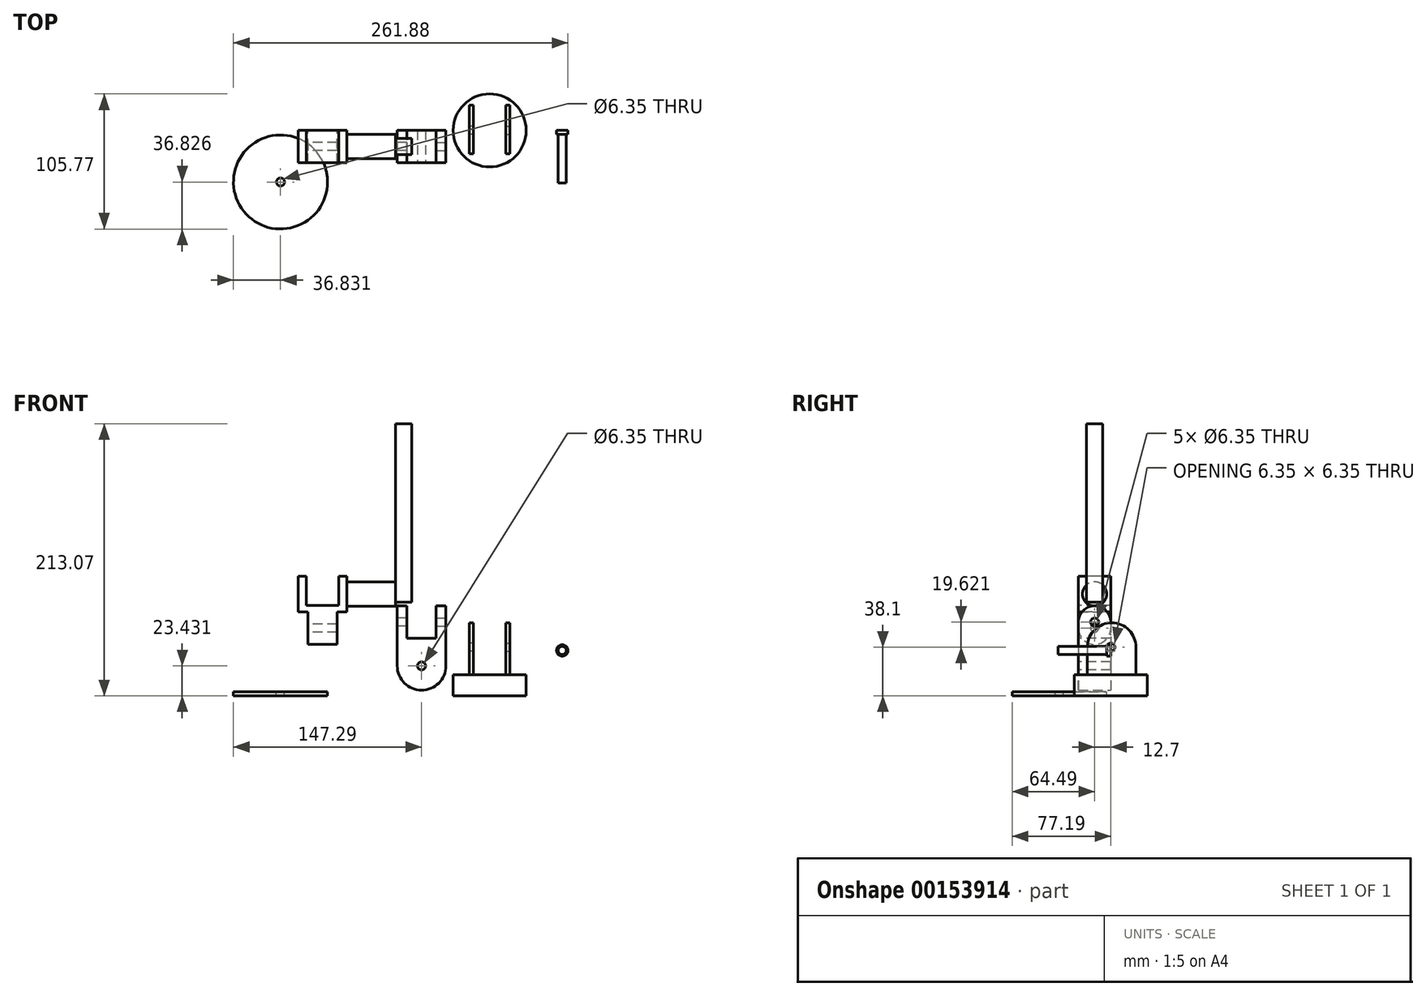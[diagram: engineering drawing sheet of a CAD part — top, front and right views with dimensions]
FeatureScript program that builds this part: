
annotation { "Feature Type Name" : "Feature", "Feature Type Description" : "" }
export const myFeature = defineFeature(function(context is Context, id is Id, definition is map)
    precondition{}
    {
        {
            var Q0;
            Q0=qCreatedBy(makeId("Top.planeOp"),FACE);
            var sketch = newSketch(context, id + "F0", { "sketchPlane" : qUnion([Q0])});
            skCircle(sketch, "E0", {"center": v(0, 0) * mm, "radius": 28.58 * mm});
            skSolve(sketch);
        }
        {
            var Q0;
            Q0 = qSketchRegion(id + "F0", true);
            extrude(context, id + "F1", {"entities" : qUnion([Q0]), "depth" : 16.5 * mm});
        }
        {
            var Q0;
            Q0=makeQuery(id+"F1.opExtrude","CAP_FACE",FACE,{"disambiguationData":[OSD([sQuery(id+"F0.wireOp",EDGE,"E0")])],"isStart":false});
            var sketch = newSketch(context, id + "F2", { "sketchPlane" : qUnion([Q0])});
            skLineSegment(sketch, "E1", {"start": v(-12.7, 19.69) * mm, "end": v(-12.7, -18.42) * mm});
            skLineSegment(sketch, "E2", {"start": v(-12.7, 19.69) * mm, "end": v(-15.88, 19.69) * mm});
            skLineSegment(sketch, "E3", {"start": v(-15.88, 19.69) * mm, "end": v(-15.88, -18.41) * mm});
            skLineSegment(sketch, "E4", {"start": v(-15.88, -18.42) * mm, "end": v(-12.7, -18.42) * mm});
            skLineSegment(sketch, "E5", {"start": v(12.7, -18.41) * mm, "end": v(12.7, 19.69) * mm});
            skLineSegment(sketch, "E6", {"start": v(12.7, 19.69) * mm, "end": v(15.88, 19.69) * mm});
            skLineSegment(sketch, "E7", {"start": v(15.88, 19.69) * mm, "end": v(15.88, -18.41) * mm});
            skLineSegment(sketch, "E8", {"start": v(15.88, -18.41) * mm, "end": v(12.7, -18.41) * mm});
            skSolve(sketch);
        }
        {
            var Q0;
            Q0 = qSketchRegion(id + "F2", true);
            extrude(context, id + "F3", {"entities" : qUnion([Q0]), "operationType" : NewBodyOperationType.ADD, "depth" : 21.59 * mm});
        }
        {
            var Q0;
            Q0=makeQuery(id+"F3.opExtrude","SWEPT_FACE",FACE,{"disambiguationData":[OSD([sQuery(id+"F2.wireOp",EDGE,"E3")])]});
            var sketch = newSketch(context, id + "F4", { "sketchPlane" : qUnion([Q0])});
            skArc(sketch, "E9", {"start": v(18.42, 38.1) * mm, "mid": v(-0.63, 57.15) * mm, "end": v(-19.69, 38.1) * mm});
            skSolve(sketch);
        }
        {
            var Q0;
            Q0=makeQuery(id+"F4.imprint","IMPRINT",FACE,{"disambiguationData":[TD([[makeQuery(id+"F4.imprint","IMPRINT",EDGE,{"derivedFrom":sQuery(id+"F4.wireOp",EDGE,"E9")}),1.0]])]});
            extrude(context, id + "F5", {"entities" : qUnion([Q0]), "operationType" : NewBodyOperationType.ADD, "oppositeDirection" : true, "depth" : 3.17 * mm});
        }
        {
            var Q0;
            Q0=makeQuery(id+"F3.opExtrude","SWEPT_FACE",FACE,{"disambiguationData":[OSD([sQuery(id+"F2.wireOp",EDGE,"E7")])]});
            var sketch = newSketch(context, id + "F6", { "sketchPlane" : qUnion([Q0])});
            skArc(sketch, "E10", {"start": v(19.68, 38.1) * mm, "mid": v(0.63, 57.15) * mm, "end": v(-18.42, 38.1) * mm});
            skSolve(sketch);
        }
        {
            var Q0;
            Q0=makeQuery(id+"F6.imprint","IMPRINT",FACE,{"disambiguationData":[TD([[makeQuery(id+"F6.imprint","IMPRINT",EDGE,{"derivedFrom":sQuery(id+"F6.wireOp",EDGE,"E10")}),1.0]])]});
            extrude(context, id + "F7", {"entities" : qUnion([Q0]), "operationType" : NewBodyOperationType.ADD, "oppositeDirection" : true, "depth" : 3.17 * mm});
        }
        {
            var Q0;
            {var subQ0=sQuery(id+"F2.wireOp",EDGE,"E7");Q0=makeQuery(id+"F7.boolean.opBoolean","MERGE",FACE,{"derivedFrom":[makeQuery(id+"F3.opExtrude","SWEPT_FACE",FACE,{"disambiguationData":[OSD([subQ0])]}),makeQuery(id+"F7.opExtrude","CAP_FACE",FACE,{"disambiguationData":[OSD([subQ0,sQuery(id+"F6.wireOp",EDGE,"E10")])],"isStart":true})]});}
            var sketch = newSketch(context, id + "F8", { "sketchPlane" : qUnion([Q0])});
            skCircle(sketch, "E11", {"center": v(0, 38.1) * mm, "radius": 3.18 * mm});
            skSolve(sketch);
        }
        {
            var Q0;
            Q0 = qSketchRegion(id + "F8", true);
            extrude(context, id + "F9", {"entities" : qUnion([Q0]), "operationType" : NewBodyOperationType.REMOVE, "oppositeDirection" : true, "depth" : 25.4 * mm});
        }
        {
            var Q0;
            {var subQ0=sQuery(id+"F2.wireOp",EDGE,"E3");Q0=makeQuery(id+"F5.boolean.opBoolean","MERGE",FACE,{"derivedFrom":[makeQuery(id+"F3.opExtrude","SWEPT_FACE",FACE,{"disambiguationData":[OSD([subQ0])]}),makeQuery(id+"F5.opExtrude","CAP_FACE",FACE,{"disambiguationData":[OSD([subQ0,sQuery(id+"F4.wireOp",EDGE,"E9")])],"isStart":true})]});}
            var sketch = newSketch(context, id + "F10", { "sketchPlane" : qUnion([Q0])});
            skCircle(sketch, "E12", {"center": v(0, 38.1) * mm, "radius": 3.18 * mm});
            skSolve(sketch);
        }
        {
            var Q0;
            Q0 = qSketchRegion(id + "F10", true);
            extrude(context, id + "F11", {"entities" : qUnion([Q0]), "operationType" : NewBodyOperationType.REMOVE, "oppositeDirection" : true, "depth" : 25.4 * mm});
        }
        {
            var Q0;
            Q0=qCreatedBy(makeId("Front.planeOp"),FACE);
            var sketch = newSketch(context, id + "F12", { "sketchPlane" : qUnion([Q0])});
            skLineSegment(sketch, "E13.bottom", {"start": v(-72.39, 57.72) * mm, "end": v(-34.29, 57.72) * mm});
            skLineSegment(sketch, "E13.top", {"start": v(-72.39, 23.43) * mm, "end": v(-34.29, 23.43) * mm});
            skLineSegment(sketch, "E13.left", {"start": v(-72.39, 57.72) * mm, "end": v(-72.39, 23.43) * mm});
            skLineSegment(sketch, "E13.right", {"start": v(-34.29, 57.72) * mm, "end": v(-34.29, 23.43) * mm});
            skArc(sketch, "E14", {"start": v(-72.39, 23.43) * mm, "mid": v(-53.34, 4.38) * mm, "end": v(-34.29, 23.43) * mm});
            skSolve(sketch);
        }
        {
            var Q0;
            Q0 = qSketchRegion(id + "F12", true);
            extrude(context, id + "F13", {"entities" : qUnion([Q0]), "depth" : 25.4 * mm});
        }
        {
            var Q0;
            Q0=makeQuery(id+"F13.opExtrude","CAP_FACE",FACE,{"disambiguationData":[OSD([sQuery(id+"F12.wireOp",EDGE,"E13.bottom"),sQuery(id+"F12.wireOp",EDGE,"E13.left"),sQuery(id+"F12.wireOp",EDGE,"E13.right"),sQuery(id+"F12.wireOp",EDGE,"E14")])],"isStart":false});
            var sketch = newSketch(context, id + "F14", { "sketchPlane" : qUnion([Q0])});
            skCircle(sketch, "E15", {"center": v(-53.34, 23.43) * mm, "radius": 3.18 * mm});
            skSolve(sketch);
        }
        {
            var Q0;
            Q0 = qSketchRegion(id + "F14", true);
            extrude(context, id + "F15", {"entities" : qUnion([Q0]), "operationType" : NewBodyOperationType.REMOVE, "oppositeDirection" : true, "depth" : 25.4 * mm});
        }
        {
            var Q0;
            Q0=makeQuery(id+"F13.opExtrude","CAP_FACE",FACE,{"disambiguationData":[OSD([sQuery(id+"F12.wireOp",EDGE,"E13.bottom"),sQuery(id+"F12.wireOp",EDGE,"E13.left"),sQuery(id+"F12.wireOp",EDGE,"E13.right"),sQuery(id+"F12.wireOp",EDGE,"E14")])],"isStart":false});
            var sketch = newSketch(context, id + "F16", { "sketchPlane" : qUnion([Q0])});
            skLineSegment(sketch, "E16.bottom", {"start": v(-64.77, 57.72) * mm, "end": v(-41.9, 57.72) * mm});
            skLineSegment(sketch, "E16.top", {"start": v(-64.77, 45.02) * mm, "end": v(-41.9, 45.02) * mm});
            skLineSegment(sketch, "E16.left", {"start": v(-64.77, 57.72) * mm, "end": v(-64.77, 45.02) * mm});
            skLineSegment(sketch, "E16.right", {"start": v(-41.9, 57.72) * mm, "end": v(-41.9, 45.02) * mm});
            skSolve(sketch);
        }
        {
            var Q0;
            Q0 = qSketchRegion(id + "F16", true);
            extrude(context, id + "F17", {"entities" : qUnion([Q0]), "operationType" : NewBodyOperationType.REMOVE, "oppositeDirection" : true, "depth" : 25.4 * mm});
        }
        {
            var Q0;
            Q0=makeQuery(id+"F13.opExtrude","SWEPT_FACE",FACE,{"disambiguationData":[OSD([sQuery(id+"F12.wireOp",EDGE,"E13.left")])]});
            var sketch = newSketch(context, id + "F18", { "sketchPlane" : qUnion([Q0])});
            skArc(sketch, "E17", {"start": v(25.4, 57.72) * mm, "mid": v(12.7, 70.42) * mm, "end": v(0, 57.72) * mm});
            skSolve(sketch);
        }
        {
            var Q0;
            Q0=makeQuery(id+"F18.imprint","IMPRINT",FACE,{"disambiguationData":[TD([[makeQuery(id+"F18.imprint","IMPRINT",EDGE,{"derivedFrom":sQuery(id+"F18.wireOp",EDGE,"E17")}),1.0]])]});
            extrude(context, id + "F19", {"entities" : qUnion([Q0]), "operationType" : NewBodyOperationType.ADD, "oppositeDirection" : true, "depth" : 7.62 * mm});
        }
        {
            var Q0;
            Q0=makeQuery(id+"F13.opExtrude","SWEPT_FACE",FACE,{"disambiguationData":[OSD([sQuery(id+"F12.wireOp",EDGE,"E13.right")])]});
            var sketch = newSketch(context, id + "F20", { "sketchPlane" : qUnion([Q0])});
            skArc(sketch, "E18", {"start": v(0, 57.72) * mm, "mid": v(-12.7, 70.42) * mm, "end": v(-25.4, 57.72) * mm});
            skSolve(sketch);
        }
        {
            var Q0;
            Q0=makeQuery(id+"F20.imprint","IMPRINT",FACE,{"disambiguationData":[TD([[makeQuery(id+"F20.imprint","IMPRINT",EDGE,{"derivedFrom":sQuery(id+"F20.wireOp",EDGE,"E18")}),1.0]])]});
            extrude(context, id + "F21", {"entities" : qUnion([Q0]), "operationType" : NewBodyOperationType.ADD, "oppositeDirection" : true, "depth" : 7.62 * mm});
        }
        {
            var Q0;
            {var subQ0=sQuery(id+"F12.wireOp",EDGE,"E13.left");Q0=makeQuery(id+"F19.boolean.opBoolean","MERGE",FACE,{"derivedFrom":[makeQuery(id+"F13.opExtrude","SWEPT_FACE",FACE,{"disambiguationData":[OSD([subQ0])]}),makeQuery(id+"F19.opExtrude","CAP_FACE",FACE,{"disambiguationData":[OSD([sQuery(id+"F12.wireOp",EDGE,"E13.bottom"),subQ0,sQuery(id+"F18.wireOp",EDGE,"E17")])],"isStart":true})]});}
            var sketch = newSketch(context, id + "F22", { "sketchPlane" : qUnion([Q0])});
            skCircle(sketch, "E19", {"center": v(12.7, 57.72) * mm, "radius": 3.18 * mm});
            skSolve(sketch);
        }
        {
            var Q0;
            Q0 = qSketchRegion(id + "F22", true);
            extrude(context, id + "F23", {"entities" : qUnion([Q0]), "operationType" : NewBodyOperationType.REMOVE, "oppositeDirection" : true, "depth" : 12.7 * mm});
        }
        {
            var Q0;
            {var subQ0=sQuery(id+"F12.wireOp",EDGE,"E13.right");Q0=makeQuery(id+"F21.boolean.opBoolean","MERGE",FACE,{"derivedFrom":[makeQuery(id+"F13.opExtrude","SWEPT_FACE",FACE,{"disambiguationData":[OSD([subQ0])]}),makeQuery(id+"F21.opExtrude","CAP_FACE",FACE,{"disambiguationData":[OSD([sQuery(id+"F12.wireOp",EDGE,"E13.bottom"),subQ0,sQuery(id+"F20.wireOp",EDGE,"E18")])],"isStart":true})]});}
            var sketch = newSketch(context, id + "F24", { "sketchPlane" : qUnion([Q0])});
            skCircle(sketch, "E20", {"center": v(-12.7, 57.72) * mm, "radius": 3.18 * mm});
            skSolve(sketch);
        }
        {
            var Q0;
            Q0 = qSketchRegion(id + "F24", true);
            extrude(context, id + "F25", {"entities" : qUnion([Q0]), "operationType" : NewBodyOperationType.REMOVE, "oppositeDirection" : true, "depth" : 25.4 * mm});
        }
        {
            var Q0;
            Q0=qCreatedBy(makeId("Front.planeOp"),FACE);
            var sketch = newSketch(context, id + "F26", { "sketchPlane" : qUnion([Q0])});
            skLineSegment(sketch, "E21.bottom", {"start": v(-142.33, 65.75) * mm, "end": v(-119.47, 65.75) * mm});
            skLineSegment(sketch, "E21.top", {"start": v(-142.33, 53.05) * mm, "end": v(-119.47, 53.05) * mm});
            skLineSegment(sketch, "E21.left", {"start": v(-142.33, 65.75) * mm, "end": v(-142.33, 53.05) * mm});
            skLineSegment(sketch, "E21.right", {"start": v(-119.47, 65.75) * mm, "end": v(-119.47, 53.05) * mm});
            skSolve(sketch);
        }
        {
            var Q0;
            Q0 = qSketchRegion(id + "F26", true);
            extrude(context, id + "F27", {"entities" : qUnion([Q0]), "depth" : 25.4 * mm});
        }
        {
            var Q0;
            Q0=makeQuery(id+"F27.opExtrude","SWEPT_FACE",FACE,{"disambiguationData":[OSD([sQuery(id+"F26.wireOp",EDGE,"E21.right")])]});
            var sketch = newSketch(context, id + "F28", { "sketchPlane" : qUnion([Q0])});
            skArc(sketch, "E22", {"start": v(-25.4, 53.05) * mm, "mid": v(-12.7, 40.35) * mm, "end": v(0, 53.05) * mm});
            skSolve(sketch);
        }
        {
            var Q0;
            Q0=makeQuery(id+"F28.imprint","IMPRINT",FACE,{"disambiguationData":[TD([[makeQuery(id+"F28.imprint","IMPRINT",EDGE,{"derivedFrom":sQuery(id+"F28.wireOp",EDGE,"E22")}),1.0]])]});
            extrude(context, id + "F29", {"entities" : qUnion([Q0]), "operationType" : NewBodyOperationType.ADD, "oppositeDirection" : true, "depth" : 22.86 * mm});
        }
        {
            var Q0;
            Q0=makeQuery(id+"F29.boolean.opBoolean","MERGE",FACE,{"derivedFrom":[makeQuery(id+"F27.opExtrude","SWEPT_FACE",FACE,{"disambiguationData":[OSD([sQuery(id+"F26.wireOp",EDGE,"E21.left")])]}),makeQuery(id+"F29.opExtrude","CAP_FACE",FACE,{"disambiguationData":[OSD([sQuery(id+"F26.wireOp",EDGE,"E21.top"),sQuery(id+"F26.wireOp",EDGE,"E21.right"),sQuery(id+"F28.wireOp",EDGE,"E22")])],"isStart":false})]});
            var sketch = newSketch(context, id + "F30", { "sketchPlane" : qUnion([Q0])});
            skCircle(sketch, "E23", {"center": v(12.7, 53.05) * mm, "radius": 3.18 * mm});
            skSolve(sketch);
        }
        {
            var Q0;
            Q0 = qSketchRegion(id + "F30", true);
            extrude(context, id + "F31", {"entities" : qUnion([Q0]), "operationType" : NewBodyOperationType.REMOVE, "oppositeDirection" : true, "depth" : 25.4 * mm});
        }
        {
            var Q0;
            Q0=makeQuery(id+"F27.opExtrude","CAP_FACE",FACE,{"disambiguationData":[OSD([sQuery(id+"F26.wireOp",EDGE,"E21.bottom"),sQuery(id+"F26.wireOp",EDGE,"E21.top"),sQuery(id+"F26.wireOp",EDGE,"E21.left"),sQuery(id+"F26.wireOp",EDGE,"E21.right")])],"isStart":false});
            var sketch = newSketch(context, id + "F32", { "sketchPlane" : qUnion([Q0])});
            skLineSegment(sketch, "E24.bottom", {"start": v(-149.95, 65.75) * mm, "end": v(-111.85, 65.75) * mm});
            skLineSegment(sketch, "E24.top", {"start": v(-149.95, 70.83) * mm, "end": v(-111.85, 70.83) * mm});
            skLineSegment(sketch, "E24.left", {"start": v(-149.95, 65.75) * mm, "end": v(-149.95, 70.83) * mm});
            skLineSegment(sketch, "E24.right", {"start": v(-111.85, 65.75) * mm, "end": v(-111.85, 70.83) * mm});
            skSolve(sketch);
        }
        {
            var Q0;
            Q0 = qSketchRegion(id + "F32", true);
            extrude(context, id + "F33", {"entities" : qUnion([Q0]), "operationType" : NewBodyOperationType.ADD, "oppositeDirection" : true, "depth" : 25.4 * mm});
        }
        {
            var Q0;
            Q0=makeQuery(id+"F33.opExtrude","SWEPT_FACE",FACE,{"disambiguationData":[OSD([sQuery(id+"F32.wireOp",EDGE,"E24.top")])]});
            var sketch = newSketch(context, id + "F34", { "sketchPlane" : qUnion([Q0])});
            skLineSegment(sketch, "E25.bottom", {"start": v(-149.95, 0) * mm, "end": v(-143.6, 0) * mm});
            skLineSegment(sketch, "E25.top", {"start": v(-149.95, -25.4) * mm, "end": v(-143.6, -25.4) * mm});
            skLineSegment(sketch, "E25.left", {"start": v(-149.95, 0) * mm, "end": v(-149.95, -25.4) * mm});
            skLineSegment(sketch, "E25.right", {"start": v(-143.6, 0) * mm, "end": v(-143.6, -25.4) * mm});
            skSolve(sketch);
        }
        {
            var Q0;
            Q0 = qSketchRegion(id + "F34", true);
            extrude(context, id + "F35", {"entities" : qUnion([Q0]), "operationType" : NewBodyOperationType.ADD, "depth" : 22.86 * mm});
        }
        {
            var Q0;
            Q0=makeQuery(id+"F33.opExtrude","SWEPT_FACE",FACE,{"disambiguationData":[OSD([sQuery(id+"F32.wireOp",EDGE,"E24.top")])]});
            var sketch = newSketch(context, id + "F36", { "sketchPlane" : qUnion([Q0])});
            skLineSegment(sketch, "E26.bottom", {"start": v(-111.85, 0) * mm, "end": v(-118.2, 0) * mm});
            skLineSegment(sketch, "E26.top", {"start": v(-111.85, -25.4) * mm, "end": v(-118.2, -25.4) * mm});
            skLineSegment(sketch, "E26.left", {"start": v(-111.85, 0) * mm, "end": v(-111.85, -25.4) * mm});
            skLineSegment(sketch, "E26.right", {"start": v(-118.2, 0) * mm, "end": v(-118.2, -25.4) * mm});
            skSolve(sketch);
        }
        {
            var Q0;
            Q0 = qSketchRegion(id + "F36", true);
            extrude(context, id + "F37", {"entities" : qUnion([Q0]), "operationType" : NewBodyOperationType.ADD, "depth" : 22.86 * mm});
        }
        {
            var Q0;
            Q0=qCreatedBy(makeId("Top.planeOp"),FACE);
            var sketch = newSketch(context, id + "F38", { "sketchPlane" : qUnion([Q0])});
            skCircle(sketch, "E27", {"center": v(-163.8, -40.36) * mm, "radius": 36.83 * mm});
            skSolve(sketch);
        }
        {
            var Q0;
            Q0 = qSketchRegion(id + "F38", true);
            extrude(context, id + "F39", {"entities" : qUnion([Q0]), "depth" : 3.3 * mm});
        }
        {
            var Q0;
            Q0=makeQuery(id+"F39.opExtrude","CAP_FACE",FACE,{"disambiguationData":[OSD([sQuery(id+"F38.wireOp",EDGE,"E27")])],"isStart":false});
            var sketch = newSketch(context, id + "F40", { "sketchPlane" : qUnion([Q0])});
            skCircle(sketch, "E28", {"center": v(-163.8, -40.36) * mm, "radius": 3.18 * mm});
            skSolve(sketch);
        }
        {
            var Q0;
            Q0 = qSketchRegion(id + "F40", true);
            extrude(context, id + "F41", {"entities" : qUnion([Q0]), "operationType" : NewBodyOperationType.REMOVE, "oppositeDirection" : true, "depth" : 25.4 * mm});
        }
        {
            var Q0;
            Q0=qCreatedBy(makeId("Front.planeOp"),FACE);
            var sketch = newSketch(context, id + "F42", { "sketchPlane" : qUnion([Q0])});
            skCircle(sketch, "E29", {"center": v(56.8, 35.48) * mm, "radius": 4.45 * mm});
            skSolve(sketch);
        }
        {
            var Q0;
            Q0 = qSketchRegion(id + "F42", true);
            extrude(context, id + "F43", {"entities" : qUnion([Q0]), "depth" : 3.17 * mm});
        }
        {
            var Q0;
            Q0=makeQuery(id+"F43.opExtrude","CAP_FACE",FACE,{"disambiguationData":[OSD([sQuery(id+"F42.wireOp",EDGE,"E29")])],"isStart":false});
            var sketch = newSketch(context, id + "F44", { "sketchPlane" : qUnion([Q0])});
            skCircle(sketch, "E30", {"center": v(56.8, 35.48) * mm, "radius": 3.18 * mm});
            skSolve(sketch);
        }
        {
            var Q0;
            Q0 = qSketchRegion(id + "F44", true);
            extrude(context, id + "F45", {"entities" : qUnion([Q0]), "operationType" : NewBodyOperationType.ADD, "depth" : 38.1 * mm});
        }
        {
            var Q0;
            Q0=makeQuery(id+"F37.boolean.opBoolean","MERGE",FACE,{"derivedFrom":[makeQuery(id+"F33.opExtrude","SWEPT_FACE",FACE,{"disambiguationData":[OSD([sQuery(id+"F32.wireOp",EDGE,"E24.right")])]}),makeQuery(id+"F37.opExtrude","SWEPT_FACE",FACE,{"disambiguationData":[OSD([sQuery(id+"F36.wireOp",EDGE,"E26.left")])]})]});
            var sketch = newSketch(context, id + "F46", { "sketchPlane" : qUnion([Q0])});
            skCircle(sketch, "E31", {"center": v(-12.7, 79.72) * mm, "radius": 9.53 * mm});
            skPoint(sketch, "E31.centerSnap0", {"position": v(-12.7, 93.69) * mm});
            skPoint(sketch, "E31.centerSnap1", {"position": v(-25.4, 79.72) * mm});
            skSolve(sketch);
        }
        {
            var Q0;
            Q0 = qSketchRegion(id + "F46", true);
            extrude(context, id + "F47", {"entities" : qUnion([Q0]), "depth" : 38.1 * mm});
        }
        {
            var Q0;
            Q0=makeQuery(id+"F47.opExtrude","CAP_FACE",FACE,{"disambiguationData":[OSD([sQuery(id+"F46.wireOp",EDGE,"E31")])],"isStart":false});
            var sketch = newSketch(context, id + "F48", { "sketchPlane" : qUnion([Q0])});
            skLineSegment(sketch, "E32.bottom", {"start": v(-6.35, 86.07) * mm, "end": v(-19.05, 86.07) * mm});
            skLineSegment(sketch, "E32.top", {"start": v(-6.35, 73.37) * mm, "end": v(-19.05, 73.37) * mm});
            skLineSegment(sketch, "E32.left", {"start": v(-6.35, 86.07) * mm, "end": v(-6.35, 73.37) * mm});
            skLineSegment(sketch, "E32.right", {"start": v(-19.05, 86.07) * mm, "end": v(-19.05, 73.37) * mm});
            skPoint(sketch, "E32.middle", {"position": v(-12.7, 79.72) * mm});
            skSolve(sketch);
        }
        {
            var Q0;
            Q0 = qSketchRegion(id + "F48", true);
            extrude(context, id + "F49", {"entities" : qUnion([Q0]), "operationType" : NewBodyOperationType.ADD, "depth" : 12.7 * mm});
        }
        {
            var Q0;
            Q0=makeQuery(id+"F49.opExtrude","SWEPT_FACE",FACE,{"disambiguationData":[OSD([sQuery(id+"F48.wireOp",EDGE,"E32.bottom")])]});
            var sketch = newSketch(context, id + "F50", { "sketchPlane" : qUnion([Q0])});
            skCircle(sketch, "E33", {"center": v(-67.4, -12.7) * mm, "radius": 6.35 * mm});
            skPoint(sketch, "E33.centerSnap0", {"position": v(-61.05, -12.7) * mm});
            skPoint(sketch, "E33.centerSnap1", {"position": v(-67.4, -19.05) * mm});
            skSolve(sketch);
        }
        {
            var Q0;
            {var subQ0=sQuery(id+"F50.wireOp",EDGE,"E33");var subQ1=sQuery(id+"F48.wireOp",EDGE,"E32.bottom");var subQ3=makeQuery(id+"F50.imprint","INTERSECT",VERTEX,{"derivedFrom":[makeQuery(id+"F49.opExtrude","CAP_EDGE",EDGE,{"disambiguationData":[OSD([subQ1])],"isStart":false}),subQ0]});Q0=makeQuery(id+"F50.imprint","IMPRINT",FACE,{"disambiguationData":[TD([[makeQuery(id+"F50.imprint","IMPRINT",EDGE,{"disambiguationData":[TD([[subQ3,-1.0]])],"derivedFrom":subQ0}),1.0]])]});}
            var Q1;
            {var subQ0=sQuery(id+"F50.wireOp",EDGE,"E33");var subQ1=sQuery(id+"F48.wireOp",EDGE,"E32.bottom");var subQ4=makeQuery(id+"F49.opExtrude","CAP_EDGE",EDGE,{"disambiguationData":[OSD([subQ1])],"isStart":true});var subQ5=makeQuery(id+"F50.imprint","INTERSECT",VERTEX,{"derivedFrom":[subQ4,subQ0]});Q1=makeQuery(id+"F50.imprint","IMPRINT",FACE,{"disambiguationData":[TD([[makeQuery(id+"F50.imprint","IMPRINT",EDGE,{"disambiguationData":[TD([[subQ5,1.0]])],"derivedFrom":subQ0}),-1.0]])]});}
            var Q2;
            {var subQ0=sQuery(id+"F50.wireOp",EDGE,"E33");var subQ1=sQuery(id+"F48.wireOp",EDGE,"E32.bottom");var subQ2=makeQuery(id+"F49.opExtrude","CAP_EDGE",EDGE,{"disambiguationData":[OSD([subQ1])],"isStart":true});var subQ3=makeQuery(id+"F50.imprint","INTERSECT",VERTEX,{"derivedFrom":[subQ2,subQ0]});Q2=makeQuery(id+"F50.imprint","IMPRINT",FACE,{"disambiguationData":[TD([[makeQuery(id+"F50.imprint","IMPRINT",EDGE,{"disambiguationData":[TD([[subQ3,-1.0]])],"derivedFrom":subQ0}),-1.0]])]});}
            extrude(context, id + "F51", {"entities" : qUnion([Q0, Q1, Q2]), "operationType" : NewBodyOperationType.ADD, "depth" : 127 * mm});
        }
    });
